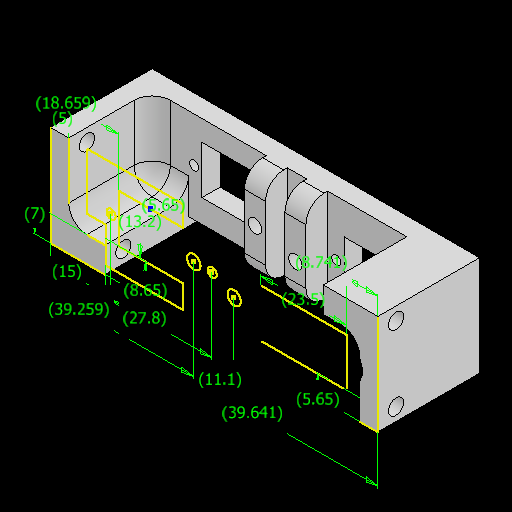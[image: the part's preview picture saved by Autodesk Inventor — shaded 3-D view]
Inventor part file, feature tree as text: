
AUTODESK INVENTOR PART (.ipt)
format: ipt  version: 2023.2 (Build 272271030, 271C)  size: 591,872 bytes
history: native  units: mm
features: sketch x8, projected_geometry x7, reference x6, extrude x5, other x5, hole x2, fillet x1
ambient origin geometry x8: Origin, YZ Plane, XZ Plane, XY Plane, X Axis, Y Axis, Z Axis, Center Point
bodies: Solid1 (feature_tree)
feature tree (34):
  extrude  "Extrusion1"  Depth=7.0mm
  hole  "Hole1"  [1 undecoded]
  extrude  "Extrusion2"  Depth=10.0mm TaperAngle=0.0deg
  extrude  "Extrusion3"  Depth=5.0mm
  extrude  "Extrusion4"  Depth=0.5mm
  hole  "Hole2"  [1 undecoded]
  extrude  "Extrusion5"  Depth=5.0mm
  fillet  "Fillet1"  Radius=5.8mm
  sketch  "Sketch8"  dims[d21=5.0mm d22=0.0mm d23=5.8mm d24=5.8mm d25=6.0mm d26=0.0mm d27=2.5mm d28=6.0mm d29=3.7mm d30=3.5mm d31=90.0deg d32=8.0mm d33=20.594885mm d34=5.0mm d35=0.0mm d36=0.0mm d37=5.0mm d38=5.65mm d39=13.2mm d40=8.65mm d41=23.5mm d42=18.658804mm d43=8.741196mm d44=5.65mm d45=5.0mm d46=15.0mm d47=7.0mm d48=27.8mm d49=11.1mm d50=39.258804mm d51=39.641196mm]
  sketch  "Sketch1"  dims[d0=27.5mm d1=7.0mm]
  sketch  "Sketch2"  dims[d2=10.0mm d3=5.0mm]
  projected_geometry  "Projected Loop1"
  sketch  "Sketch3"  dims[d4=70.0mm d5=10.0mm d6=0.0mm]
  projected_geometry  "Projected Loop2"
  projected_geometry  "Projected Loop3"
  sketch  "Sketch4"  dims[d7=20.45mm]
  projected_geometry  "Projected Loop4"
  projected_geometry  "Projected Loop5"
  reference  "Reference1"
  reference  "Reference2"
  reference  "Reference3"
  reference  "Reference4"
  sketch  "Sketch5"  dims[d8=4.2mm d9=6.0mm d10=4.5mm d11=2.5mm d12=90.0deg d13=8.0mm d14=20.594885mm d15=5.0mm]
  reference  "Reference5"
  reference  "Reference6"
  projected_geometry  "Projected Loop6"
  sketch  "Sketch6"  dims[d16=17.95mm d17=0.0mm d18=0.5mm]
  sketch  "Sketch7"  dims[d19=0.5mm d20=2.5mm]
  projected_geometry  "Projected Loop7"
  other  "Horizontal Leg Test v3.iam"
  other  "SG90 - Micro Servo 9g - Tower Pro:2"
  other  "SG90 - Micro Servo 9g - Tower Pro:1"
  other  "Intermediate Gear:2"
  other  "Intermediate Gear:1"
note: 2 required parameter values undecoded (feature->parameter linkage not recoverable at this tier; creation-order binding heuristic only, values carry confidence <= 0.55)
